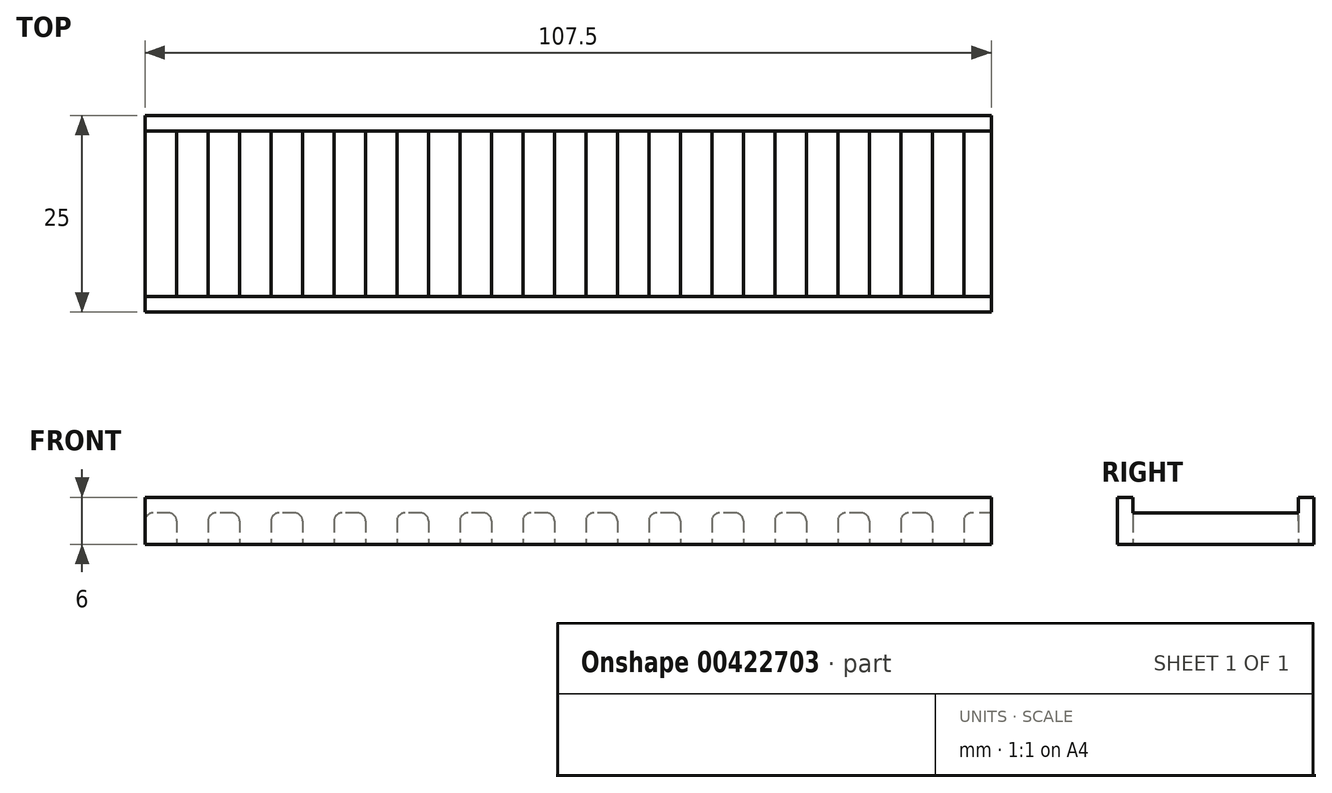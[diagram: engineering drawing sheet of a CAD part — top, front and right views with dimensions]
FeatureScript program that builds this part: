
annotation { "Feature Type Name" : "Feature", "Feature Type Description" : "" }
export const myFeature = defineFeature(function(context is Context, id is Id, definition is map)
    precondition{}
    {
        {
            var Q0;
            Q0=qCreatedBy(makeId("Top.planeOp"),FACE);
            var sketch = newSketch(context, id + "F0", { "sketchPlane" : qUnion([Q0])});
            skLineSegment(sketch, "E0", {"start": v(0, 25) * mm, "end": v(0, 0) * mm});
            skLineSegment(sketch, "E1.0", {"start": v(4, 23) * mm, "end": v(4, 2) * mm});
            skLineSegment(sketch, "E2.0", {"start": v(8, 23) * mm, "end": v(8, 2) * mm});
            skLineSegment(sketch, "E3.0", {"start": v(12, 23) * mm, "end": v(12, 2) * mm});
            skLineSegment(sketch, "E4.0", {"start": v(16, 23) * mm, "end": v(16, 2) * mm});
            skLineSegment(sketch, "E5.0", {"start": v(20, 23) * mm, "end": v(20, 2) * mm});
            skLineSegment(sketch, "E6.0", {"start": v(24, 23) * mm, "end": v(24, 2) * mm});
            skLineSegment(sketch, "E7.0", {"start": v(28, 23) * mm, "end": v(28, 2) * mm});
            skLineSegment(sketch, "E8.0", {"start": v(32, 23) * mm, "end": v(32, 2) * mm});
            skLineSegment(sketch, "E9.0", {"start": v(36, 23) * mm, "end": v(36, 2) * mm});
            skLineSegment(sketch, "E10.0", {"start": v(40, 23) * mm, "end": v(40, 2) * mm});
            skLineSegment(sketch, "E11.0", {"start": v(44, 23) * mm, "end": v(44, 2) * mm});
            skLineSegment(sketch, "E12.0", {"start": v(48, 23) * mm, "end": v(48, 2) * mm});
            skLineSegment(sketch, "E13.0", {"start": v(52, 23) * mm, "end": v(52, 2) * mm});
            skLineSegment(sketch, "E14.0", {"start": v(56, 23) * mm, "end": v(56, 2) * mm});
            skLineSegment(sketch, "E15.0", {"start": v(60, 23) * mm, "end": v(60, 2) * mm});
            skLineSegment(sketch, "E16.0", {"start": v(64, 23) * mm, "end": v(64, 2) * mm});
            skLineSegment(sketch, "E17.0", {"start": v(72, 23) * mm, "end": v(72, 2) * mm});
            skLineSegment(sketch, "E18.0", {"start": v(72, 23) * mm, "end": v(68, 23) * mm});
            skLineSegment(sketch, "E19.0", {"start": v(4, 2) * mm, "end": v(8, 2) * mm});
            skLineSegment(sketch, "E20.trimOffspring", {"start": v(64, 23) * mm, "end": v(60, 23) * mm});
            skLineSegment(sketch, "E21.trimOffspring", {"start": v(68, 2) * mm, "end": v(72, 2) * mm});
            skLineSegment(sketch, "E22.trimOffspring", {"start": v(60, 2) * mm, "end": v(64, 2) * mm});
            skLineSegment(sketch, "E23.trimOffspring", {"start": v(56, 23) * mm, "end": v(52, 23) * mm});
            skLineSegment(sketch, "E24.trimOffspring", {"start": v(48, 23) * mm, "end": v(44, 23) * mm});
            skLineSegment(sketch, "E25.trimOffspring", {"start": v(52, 2) * mm, "end": v(56, 2) * mm});
            skLineSegment(sketch, "E26.trimOffspring", {"start": v(44, 2) * mm, "end": v(48, 2) * mm});
            skLineSegment(sketch, "E27.trimOffspring", {"start": v(40, 23) * mm, "end": v(36, 23) * mm});
            skLineSegment(sketch, "E28.trimOffspring", {"start": v(32, 23) * mm, "end": v(28, 23) * mm});
            skLineSegment(sketch, "E29.trimOffspring", {"start": v(36, 2) * mm, "end": v(40, 2) * mm});
            skLineSegment(sketch, "E30.trimOffspring", {"start": v(28, 2) * mm, "end": v(32, 2) * mm});
            skLineSegment(sketch, "E31.trimOffspring", {"start": v(24, 23) * mm, "end": v(20, 23) * mm});
            skLineSegment(sketch, "E32.trimOffspring", {"start": v(16, 23) * mm, "end": v(12, 23) * mm});
            skLineSegment(sketch, "E33.trimOffspring", {"start": v(20, 2) * mm, "end": v(24, 2) * mm});
            skLineSegment(sketch, "E34.trimOffspring", {"start": v(12, 2) * mm, "end": v(16, 2) * mm});
            skLineSegment(sketch, "E35.trimOffspring", {"start": v(8, 23) * mm, "end": v(4, 23) * mm});
            skLineSegment(sketch, "E36", {"start": v(0, 25) * mm, "end": v(107.5, 25) * mm});
            skLineSegment(sketch, "E37", {"start": v(0, 0) * mm, "end": v(107.5, 0) * mm});
            skLineSegment(sketch, "E38", {"start": v(107.5, 0) * mm, "end": v(107.5, 25) * mm});
            skLineSegment(sketch, "E39", {"start": v(68, 2) * mm, "end": v(68, 23) * mm});
            skLineSegment(sketch, "E40.0", {"start": v(76, 23) * mm, "end": v(76, 2) * mm});
            skLineSegment(sketch, "E41.0", {"start": v(80, 23) * mm, "end": v(80, 2) * mm});
            skLineSegment(sketch, "E42.0", {"start": v(84, 23) * mm, "end": v(84, 2) * mm});
            skLineSegment(sketch, "E43.0", {"start": v(88, 23) * mm, "end": v(88, 2) * mm});
            skLineSegment(sketch, "E44.0", {"start": v(92, 23) * mm, "end": v(92, 2) * mm});
            skLineSegment(sketch, "E45.0", {"start": v(96, 23) * mm, "end": v(96, 2) * mm});
            skLineSegment(sketch, "E46.0", {"start": v(100, 23) * mm, "end": v(100, 2) * mm});
            skLineSegment(sketch, "E47.0", {"start": v(104, 23) * mm, "end": v(104, 2) * mm});
            skLineSegment(sketch, "E48", {"start": v(76, 23) * mm, "end": v(80, 23) * mm});
            skLineSegment(sketch, "E49", {"start": v(84, 23) * mm, "end": v(88, 23) * mm});
            skLineSegment(sketch, "E50", {"start": v(92, 23) * mm, "end": v(96, 23) * mm});
            skLineSegment(sketch, "E51", {"start": v(100, 23) * mm, "end": v(104, 23) * mm});
            skLineSegment(sketch, "E52", {"start": v(76, 2) * mm, "end": v(80, 2) * mm});
            skLineSegment(sketch, "E53", {"start": v(84, 2) * mm, "end": v(88, 2) * mm});
            skLineSegment(sketch, "E54", {"start": v(92, 2) * mm, "end": v(96, 2) * mm});
            skLineSegment(sketch, "E55", {"start": v(100, 2) * mm, "end": v(104, 2) * mm});
            skSolve(sketch);
        }
        {
            var Q0;
            Q0=qSketchRegion(id+"F0",true);
            extrude(context, id + "F1", {"entities" : qUnion([Q0]), "depth" : 4 * mm});
        }
        {
            var Q0;
            Q0=makeQuery(id+"F1.opExtrude","CAP_EDGE",EDGE,{"disambiguationData":[OSD([sQuery(id+"F0.wireOp",EDGE,"E2.0")])],"isStart":false});
            var Q1;
            Q1=makeQuery(id+"F1.opExtrude","CAP_EDGE",EDGE,{"disambiguationData":[OSD([sQuery(id+"F0.wireOp",EDGE,"E3.0")])],"isStart":false});
            var Q2;
            Q2=makeQuery(id+"F1.opExtrude","CAP_EDGE",EDGE,{"disambiguationData":[OSD([sQuery(id+"F0.wireOp",EDGE,"E4.0")])],"isStart":false});
            var Q3;
            Q3=makeQuery(id+"F1.opExtrude","CAP_EDGE",EDGE,{"disambiguationData":[OSD([sQuery(id+"F0.wireOp",EDGE,"E5.0")])],"isStart":false});
            var Q4;
            Q4=makeQuery(id+"F1.opExtrude","CAP_EDGE",EDGE,{"disambiguationData":[OSD([sQuery(id+"F0.wireOp",EDGE,"E6.0")])],"isStart":false});
            var Q5;
            Q5=makeQuery(id+"F1.opExtrude","CAP_EDGE",EDGE,{"disambiguationData":[OSD([sQuery(id+"F0.wireOp",EDGE,"E7.0")])],"isStart":false});
            var Q6;
            Q6=makeQuery(id+"F1.opExtrude","CAP_EDGE",EDGE,{"disambiguationData":[OSD([sQuery(id+"F0.wireOp",EDGE,"E8.0")])],"isStart":false});
            var Q7;
            Q7=makeQuery(id+"F1.opExtrude","CAP_EDGE",EDGE,{"disambiguationData":[OSD([sQuery(id+"F0.wireOp",EDGE,"E9.0")])],"isStart":false});
            var Q8;
            Q8=makeQuery(id+"F1.opExtrude","CAP_EDGE",EDGE,{"disambiguationData":[OSD([sQuery(id+"F0.wireOp",EDGE,"E10.0")])],"isStart":false});
            var Q9;
            Q9=makeQuery(id+"F1.opExtrude","CAP_EDGE",EDGE,{"disambiguationData":[OSD([sQuery(id+"F0.wireOp",EDGE,"E11.0")])],"isStart":false});
            var Q10;
            Q10=makeQuery(id+"F1.opExtrude","CAP_EDGE",EDGE,{"disambiguationData":[OSD([sQuery(id+"F0.wireOp",EDGE,"E12.0")])],"isStart":false});
            var Q11;
            Q11=makeQuery(id+"F1.opExtrude","CAP_EDGE",EDGE,{"disambiguationData":[OSD([sQuery(id+"F0.wireOp",EDGE,"E13.0")])],"isStart":false});
            var Q12;
            Q12=makeQuery(id+"F1.opExtrude","CAP_EDGE",EDGE,{"disambiguationData":[OSD([sQuery(id+"F0.wireOp",EDGE,"E14.0")])],"isStart":false});
            var Q13;
            Q13=makeQuery(id+"F1.opExtrude","CAP_EDGE",EDGE,{"disambiguationData":[OSD([sQuery(id+"F0.wireOp",EDGE,"E15.0")])],"isStart":false});
            var Q14;
            Q14=makeQuery(id+"F1.opExtrude","CAP_EDGE",EDGE,{"disambiguationData":[OSD([sQuery(id+"F0.wireOp",EDGE,"E16.0")])],"isStart":false});
            var Q15;
            Q15=makeQuery(id+"F1.opExtrude","CAP_EDGE",EDGE,{"disambiguationData":[OSD([sQuery(id+"F0.wireOp",EDGE,"b9decff6-60c3-44e2-a8f9-30329346e0b0.0")])],"isStart":false});
            var Q16;
            Q16=makeQuery(id+"F1.opExtrude","CAP_EDGE",EDGE,{"disambiguationData":[OSD([sQuery(id+"F0.wireOp",EDGE,"E39")])],"isStart":false});
            var Q17;
            Q17=makeQuery(id+"F1.opExtrude","CAP_EDGE",EDGE,{"disambiguationData":[OSD([sQuery(id+"F0.wireOp",EDGE,"E17.0")])],"isStart":false});
            var Q18;
            Q18=makeQuery(id+"F1.opExtrude","CAP_EDGE",EDGE,{"disambiguationData":[OSD([sQuery(id+"F0.wireOp",EDGE,"E40.0")])],"isStart":false});
            var Q19;
            Q19=makeQuery(id+"F1.opExtrude","CAP_EDGE",EDGE,{"disambiguationData":[OSD([sQuery(id+"F0.wireOp",EDGE,"E41.0")])],"isStart":false});
            var Q20;
            Q20=makeQuery(id+"F1.opExtrude","CAP_EDGE",EDGE,{"disambiguationData":[OSD([sQuery(id+"F0.wireOp",EDGE,"E42.0")])],"isStart":false});
            var Q21;
            Q21=makeQuery(id+"F1.opExtrude","CAP_EDGE",EDGE,{"disambiguationData":[OSD([sQuery(id+"F0.wireOp",EDGE,"E43.0")])],"isStart":false});
            var Q22;
            Q22=makeQuery(id+"F1.opExtrude","CAP_EDGE",EDGE,{"disambiguationData":[OSD([sQuery(id+"F0.wireOp",EDGE,"E44.0")])],"isStart":false});
            var Q23;
            Q23=makeQuery(id+"F1.opExtrude","CAP_EDGE",EDGE,{"disambiguationData":[OSD([sQuery(id+"F0.wireOp",EDGE,"E45.0")])],"isStart":false});
            var Q24;
            Q24=makeQuery(id+"F1.opExtrude","CAP_EDGE",EDGE,{"disambiguationData":[OSD([sQuery(id+"F0.wireOp",EDGE,"E46.0")])],"isStart":false});
            var Q25;
            Q25=makeQuery(id+"F1.opExtrude","CAP_EDGE",EDGE,{"disambiguationData":[OSD([sQuery(id+"F0.wireOp",EDGE,"E47.0")])],"isStart":false});
            fillet(context, id + "F2", {"entities" : qUnion([Q0, Q1, Q2, Q3, Q4, Q5, Q6, Q7, Q8, Q9, Q10, Q11, Q12, Q13, Q14, Q15, Q16, Q17, Q18, Q19, Q20, Q21, Q22, Q23, Q24, Q25]), "radius" : 1 * mm, "tangentPropagation" : true, "allowEdgeOverflow" : false});
        }
        {
            var Q0;
            Q0=makeQuery(id+"F1.opExtrude","CAP_FACE",FACE,{"disambiguationData":[OSD([sQuery(id+"F0.wireOp",EDGE,"IT1JtDfS-6wem-IC5y-MfDq-X7xjbZjFhjaX"),sQuery(id+"F0.wireOp",EDGE,"CtWnb4rl-nCio-51gJ-VG3f-wIze3EkkuYtm"),sQuery(id+"F0.wireOp",EDGE,"4tLn85YO-20ms-TKEU-XhFj-JpR1JimQEEGb"),sQuery(id+"F0.wireOp",EDGE,"E0"),sQuery(id+"F0.wireOp",EDGE,"E1.0"),sQuery(id+"F0.wireOp",EDGE,"E2.0"),sQuery(id+"F0.wireOp",EDGE,"E3.0"),sQuery(id+"F0.wireOp",EDGE,"E4.0"),sQuery(id+"F0.wireOp",EDGE,"E5.0"),sQuery(id+"F0.wireOp",EDGE,"E6.0"),sQuery(id+"F0.wireOp",EDGE,"E7.0"),sQuery(id+"F0.wireOp",EDGE,"E8.0"),sQuery(id+"F0.wireOp",EDGE,"E9.0"),sQuery(id+"F0.wireOp",EDGE,"E10.0"),sQuery(id+"F0.wireOp",EDGE,"E11.0"),sQuery(id+"F0.wireOp",EDGE,"E12.0"),sQuery(id+"F0.wireOp",EDGE,"E13.0"),sQuery(id+"F0.wireOp",EDGE,"E14.0"),sQuery(id+"F0.wireOp",EDGE,"E15.0"),sQuery(id+"F0.wireOp",EDGE,"E16.0"),sQuery(id+"F0.wireOp",EDGE,"b9decff6-60c3-44e2-a8f9-30329346e0b0.0"),sQuery(id+"F0.wireOp",EDGE,"E17.0"),sQuery(id+"F0.wireOp",EDGE,"E18.0"),sQuery(id+"F0.wireOp",EDGE,"E19.0"),sQuery(id+"F0.wireOp",EDGE,"E20.trimOffspring"),sQuery(id+"F0.wireOp",EDGE,"E21.trimOffspring"),sQuery(id+"F0.wireOp",EDGE,"E22.trimOffspring"),sQuery(id+"F0.wireOp",EDGE,"E23.trimOffspring"),sQuery(id+"F0.wireOp",EDGE,"E24.trimOffspring"),sQuery(id+"F0.wireOp",EDGE,"E25.trimOffspring"),sQuery(id+"F0.wireOp",EDGE,"E26.trimOffspring"),sQuery(id+"F0.wireOp",EDGE,"E27.trimOffspring"),sQuery(id+"F0.wireOp",EDGE,"E28.trimOffspring"),sQuery(id+"F0.wireOp",EDGE,"E29.trimOffspring"),sQuery(id+"F0.wireOp",EDGE,"E30.trimOffspring"),sQuery(id+"F0.wireOp",EDGE,"E31.trimOffspring"),sQuery(id+"F0.wireOp",EDGE,"E32.trimOffspring"),sQuery(id+"F0.wireOp",EDGE,"E33.trimOffspring"),sQuery(id+"F0.wireOp",EDGE,"E34.trimOffspring"),sQuery(id+"F0.wireOp",EDGE,"E35.trimOffspring")])],"isStart":false});
            var sketch = newSketch(context, id + "F3", { "sketchPlane" : qUnion([Q0])});
            skLineSegment(sketch, "E56", {"start": v(107.5, 2) * mm, "end": v(0, 2) * mm});
            skLineSegment(sketch, "E57", {"start": v(107.5, 23) * mm, "end": v(0, 23) * mm});
            skLineSegment(sketch, "E58", {"start": v(0, 23) * mm, "end": v(0, 25) * mm});
            skLineSegment(sketch, "E59", {"start": v(0, 25) * mm, "end": v(107.5, 25) * mm});
            skLineSegment(sketch, "E60", {"start": v(0, 25) * mm, "end": v(0, 2) * mm});
            skLineSegment(sketch, "E61", {"start": v(107.5, 25) * mm, "end": v(107.5, 23) * mm});
            skLineSegment(sketch, "E62", {"start": v(0, 2) * mm, "end": v(0, 0) * mm});
            skLineSegment(sketch, "E63", {"start": v(0, 0) * mm, "end": v(107.5, 0) * mm});
            skLineSegment(sketch, "E64", {"start": v(107.5, 0) * mm, "end": v(107.5, 2) * mm});
            skSolve(sketch);
        }
        {
            var Q0;
            Q0=qSketchRegion(id+"F3",true);
            extrude(context, id + "F4", {"entities" : qUnion([Q0]), "operationType" : NewBodyOperationType.ADD, "depth" : 2 * mm});
        }
        {
            var Q0;
            Q0=makeQuery(id+"F1.opExtrude","CAP_EDGE",EDGE,{"disambiguationData":[OSD([sQuery(id+"F0.wireOp",EDGE,"E1.0")])],"isStart":false});
            var Q1;
            Q1=makeQuery(id+"F1.opExtrude","CAP_EDGE",EDGE,{"disambiguationData":[OSD([sQuery(id+"F0.wireOp",EDGE,"E0")])],"isStart":false});
            fillet(context, id + "F5", {"entities" : qUnion([Q0, Q1]), "radius" : 1 * mm, "tangentPropagation" : true, "allowEdgeOverflow" : false});
        }
    });
